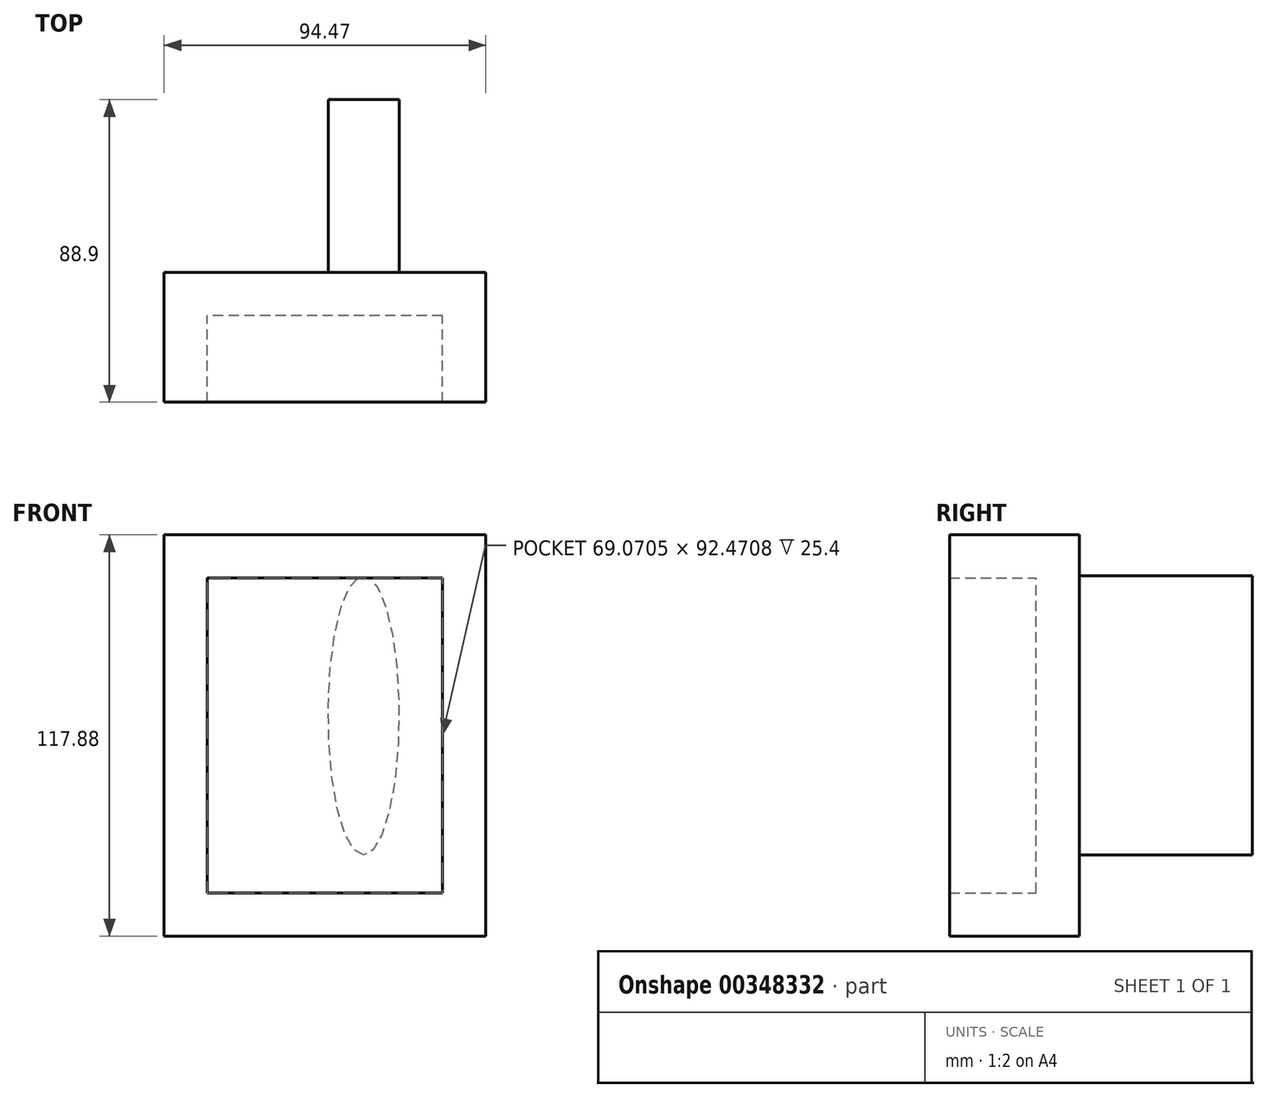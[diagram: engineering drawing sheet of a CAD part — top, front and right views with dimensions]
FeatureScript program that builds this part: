
annotation { "Feature Type Name" : "Feature", "Feature Type Description" : "" }
export const myFeature = defineFeature(function(context is Context, id is Id, definition is map)
    precondition{}
    {
        {
            var Q0;
            Q0=qCreatedBy(makeId("Front.planeOp"),FACE);
            var sketch = newSketch(context, id + "F0", { "sketchPlane" : qUnion([Q0])});
            skLineSegment(sketch, "E0.bottom", {"start": v(79.68, -52.14) * mm, "end": v(10.6, -52.14) * mm});
            skLineSegment(sketch, "E0.top", {"start": v(79.68, 40.34) * mm, "end": v(10.6, 40.34) * mm});
            skLineSegment(sketch, "E0.left", {"start": v(79.68, -52.14) * mm, "end": v(79.68, 40.34) * mm});
            skLineSegment(sketch, "E0.right", {"start": v(10.6, -52.14) * mm, "end": v(10.6, 40.34) * mm});
            skSolve(sketch);
        }
        {
            var Q0;
            Q0=makeQuery(id+"F0.imprint","IMPRINT",FACE,{"disambiguationData":[TD([[makeQuery(id+"F0.imprint","IMPRINT",EDGE,{"derivedFrom":sQuery(id+"F0.wireOp",EDGE,"E0.bottom")}),-1.0]])]});
            extrude(context, id + "F1", {"entities" : qUnion([Q0]), "depth" : 25.4 * mm});
        }
        {
            var Q0;
            Q0=makeQuery(id+"F1.opExtrude","CAP_FACE",FACE,{"disambiguationData":[OSD([sQuery(id+"F0.wireOp",EDGE,"E0.bottom"),sQuery(id+"F0.wireOp",EDGE,"E0.top"),sQuery(id+"F0.wireOp",EDGE,"E0.left"),sQuery(id+"F0.wireOp",EDGE,"E0.right")])],"isStart":false});
            shell(context, id + "F2", {"entities" : qUnion([Q0]), "thickness" : 12.7 * mm, "oppositeDirection" : true});
        }
        {
            var Q0;
            Q0=makeQuery(id+"F1.opExtrude","CAP_FACE",FACE,{"disambiguationData":[OSD([sQuery(id+"F0.wireOp",EDGE,"E0.bottom"),sQuery(id+"F0.wireOp",EDGE,"E0.top"),sQuery(id+"F0.wireOp",EDGE,"E0.left"),sQuery(id+"F0.wireOp",EDGE,"E0.right")])],"isStart":true});
            var sketch = newSketch(context, id + "F3", { "sketchPlane" : qUnion([Q0])});
            skPoint(sketch, "E1", {"position": v(-92.38, 16.54) * mm});
            skPoint(sketch, "E2", {"position": v(-92.38, -29.46) * mm});
            skPoint(sketch, "E3", {"position": v(-43.21, 41.27) * mm});
            skPoint(sketch, "E4", {"position": v(-44.02, -33.13) * mm});
            skPoint(sketch, "E5", {"position": v(-10.6, 14.93) * mm});
            skSolve(sketch);
        }
        {
            var Q0;
            Q0=makeQuery(id+"F3.imprint","IMPRINT",FACE,{"disambiguationData":[TD([[makeQuery(id+"F3.imprint","IMPRINT",EDGE,{"derivedFrom":makeQuery(id+"F1.opExtrude","CAP_EDGE",EDGE,{"disambiguationData":[OSD([sQuery(id+"F0.wireOp",EDGE,"E0.bottom")])],"isStart":true})}),1.0]])]});
            var sketch = newSketch(context, id + "F4", { "sketchPlane" : qUnion([Q0])});
            skEllipse(sketch, "E6", {"center": v(-56.5, 0) * mm, "majorRadius": 41.05 * mm, "minorRadius": 10.4 * mm, "majorAxis": v(0, -1)});
            skSolve(sketch);
        }
        {
            var Q0;
            Q0=makeQuery(id+"F4.imprint","IMPRINT",FACE,{"disambiguationData":[TD([[makeQuery(id+"F4.imprint","IMPRINT",EDGE,{"derivedFrom":sQuery(id+"F4.wireOp",EDGE,"E6")}),1.0]])]});
            var Q1;
            Q1 = qSketchRegion(id + "F4", true);
            extrude(context, id + "F5", {"entities" : qUnion([Q0, Q1]), "operationType" : NewBodyOperationType.ADD, "depth" : 50.8 * mm});
        }
    });
